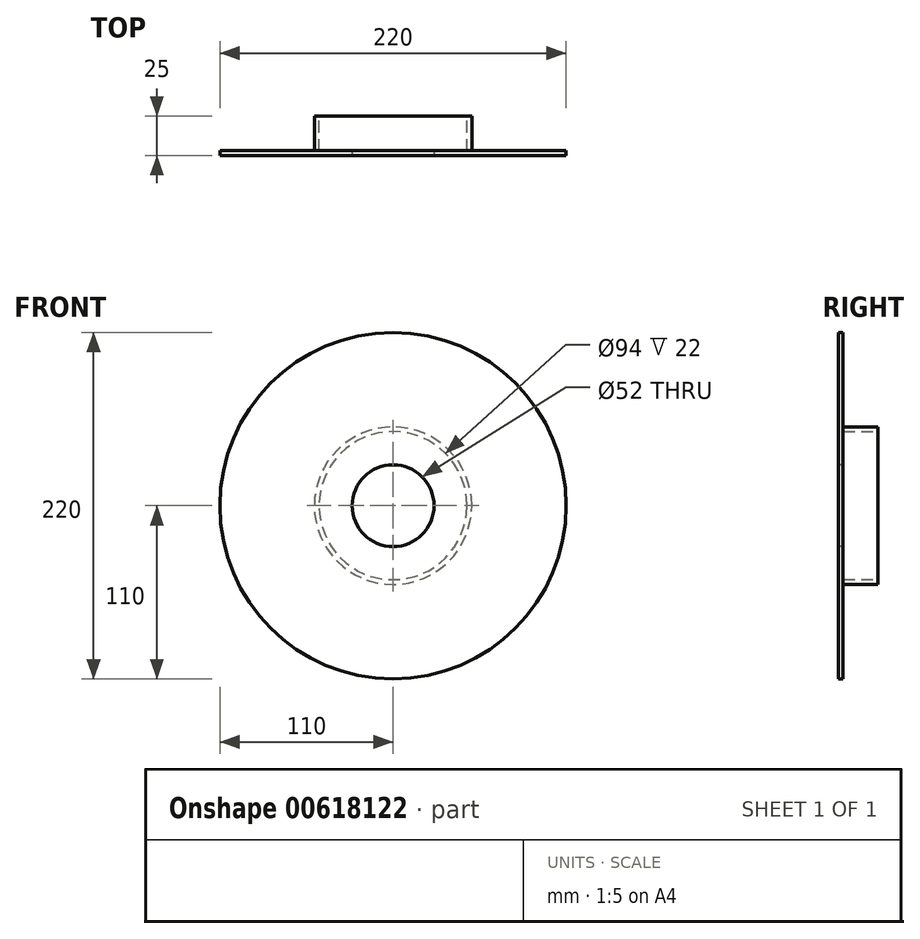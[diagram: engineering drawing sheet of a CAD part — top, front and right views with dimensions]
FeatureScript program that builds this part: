
annotation { "Feature Type Name" : "Feature", "Feature Type Description" : "" }
export const myFeature = defineFeature(function(context is Context, id is Id, definition is map)
    precondition{}
    {
        {
            var Q0;
            Q0=qCreatedBy(makeId("Front.planeOp"),FACE);
            var sketch = newSketch(context, id + "F0", { "sketchPlane" : qUnion([Q0])});
            skCircle(sketch, "E0", {"center": v(0, 0) * mm, "radius": 50 * mm});
            skCircle(sketch, "E1.0", {"center": v(0, 0) * mm, "radius": 47 * mm});
            skCircle(sketch, "E2", {"center": v(0, 0) * mm, "radius": 48.5 * mm});
            skLineSegment(sketch, "E3", {"start": v(0, 47) * mm, "end": v(0, 50) * mm});
            skLineSegment(sketch, "E4", {"start": v(33.23, 33.23) * mm, "end": v(35.36, 35.36) * mm});
            skLineSegment(sketch, "E5.1.0", {"start": v(-47, 0) * mm, "end": v(-50, 0) * mm});
            skLineSegment(sketch, "E5.1.1", {"start": v(-33.23, 33.23) * mm, "end": v(-35.36, 35.36) * mm});
            skLineSegment(sketch, "E5.2.0", {"start": v(0, -47) * mm, "end": v(0, -50) * mm});
            skLineSegment(sketch, "E5.2.1", {"start": v(-33.23, -33.23) * mm, "end": v(-35.36, -35.36) * mm});
            skLineSegment(sketch, "E5.3.0", {"start": v(47, 0) * mm, "end": v(50, 0) * mm});
            skLineSegment(sketch, "E5.3.1", {"start": v(33.23, -33.23) * mm, "end": v(35.36, -35.36) * mm});
            skSolve(sketch);
        }
        {
            var Q0;
            Q0=makeQuery(id+"F0.imprint","IMPRINT",FACE,{"disambiguationData":[TD([[makeQuery(id+"F0.imprint","IMPRINT",EDGE,{"derivedFrom":sQuery(id+"F0.wireOp",EDGE,"E0")}),1.0]])]});
            var Q1;
            {var subQ0=sQuery(id+"F0.wireOp",EDGE,"E3");var subQ1=sQuery(id+"F0.wireOp",EDGE,"E1.0");var subQ2=makeQuery(id+"F0.imprint","INTERSECT",VERTEX,{"derivedFrom":[subQ1,subQ0]});Q1=makeQuery(id+"F0.imprint","IMPRINT",FACE,{"disambiguationData":[TD([[makeQuery(id+"F0.imprint","IMPRINT",EDGE,{"disambiguationData":[TD([[subQ2,-1.0]])],"derivedFrom":subQ1}),-1.0]])]});}
            var Q2;
            {var subQ0=sQuery(id+"F0.wireOp",EDGE,"ee602be9-f56a-464f-86fb-2bc137bb6036.1.0");var subQ1=sQuery(id+"F0.wireOp",EDGE,"E1.0");var subQ2=makeQuery(id+"F0.imprint","INTERSECT",VERTEX,{"derivedFrom":[subQ1,subQ0]});Q2=makeQuery(id+"F0.imprint","IMPRINT",FACE,{"disambiguationData":[TD([[makeQuery(id+"F0.imprint","IMPRINT",EDGE,{"disambiguationData":[TD([[subQ2,1.0]])],"derivedFrom":subQ1}),-1.0]])]});}
            var Q3;
            {var subQ0=sQuery(id+"F0.wireOp",EDGE,"ee602be9-f56a-464f-86fb-2bc137bb6036.1.0");var subQ1=sQuery(id+"F0.wireOp",EDGE,"E1.0");var subQ2=makeQuery(id+"F0.imprint","INTERSECT",VERTEX,{"derivedFrom":[subQ1,subQ0]});Q3=makeQuery(id+"F0.imprint","IMPRINT",FACE,{"disambiguationData":[TD([[makeQuery(id+"F0.imprint","IMPRINT",EDGE,{"disambiguationData":[TD([[subQ2,-1.0]])],"derivedFrom":subQ1}),-1.0]])]});}
            var Q4;
            {var subQ0=sQuery(id+"F0.wireOp",EDGE,"E3");var subQ1=sQuery(id+"F0.wireOp",EDGE,"E1.0");var subQ2=makeQuery(id+"F0.imprint","INTERSECT",VERTEX,{"derivedFrom":[subQ1,subQ0]});Q4=makeQuery(id+"F0.imprint","IMPRINT",FACE,{"disambiguationData":[TD([[makeQuery(id+"F0.imprint","IMPRINT",EDGE,{"disambiguationData":[TD([[subQ2,1.0]])],"derivedFrom":subQ1}),-1.0]])]});}
            var Q5;
            {var subQ0=sQuery(id+"F0.wireOp",EDGE,"ee602be9-f56a-464f-86fb-2bc137bb6036.2.0");var subQ1=sQuery(id+"F0.wireOp",EDGE,"E1.0");var subQ2=makeQuery(id+"F0.imprint","INTERSECT",VERTEX,{"derivedFrom":[subQ1,subQ0]});Q5=makeQuery(id+"F0.imprint","IMPRINT",FACE,{"disambiguationData":[TD([[makeQuery(id+"F0.imprint","IMPRINT",EDGE,{"disambiguationData":[TD([[subQ2,1.0]])],"derivedFrom":subQ1}),-1.0]])]});}
            var Q6;
            {var subQ0=sQuery(id+"F0.wireOp",EDGE,"E4");var subQ1=sQuery(id+"F0.wireOp",EDGE,"E1.0");var subQ2=makeQuery(id+"F0.imprint","INTERSECT",VERTEX,{"derivedFrom":[subQ1,subQ0]});Q6=makeQuery(id+"F0.imprint","IMPRINT",FACE,{"disambiguationData":[TD([[makeQuery(id+"F0.imprint","IMPRINT",EDGE,{"disambiguationData":[TD([[subQ2,1.0]])],"derivedFrom":subQ1}),-1.0]])]});}
            extrude(context, id + "F1", {"entities" : qUnion([Q0, Q1, Q2, Q3, Q4, Q5, Q6]), "depth" : 22 * mm, "offsetDistance" : 25 * mm});
        }
        {
            var Q0;
            Q0=makeQuery(id+"F1.opExtrude","CAP_FACE",FACE,{"disambiguationData":[OSD([sQuery(id+"F0.wireOp",EDGE,"E0")])],"isStart":false});
            var sketch = newSketch(context, id + "F2", { "sketchPlane" : qUnion([Q0])});
            skPoint(sketch, "E6.0", {"position": v(0, 0) * mm});
            skCircle(sketch, "E7", {"center": v(0, 0) * mm, "radius": 110 * mm});
            skSolve(sketch);
        }
        {
            var Q0;
            Q0=makeQuery(id+"F2.imprint","IMPRINT",FACE,{"disambiguationData":[TD([[makeQuery(id+"F2.imprint","IMPRINT",EDGE,{"derivedFrom":sQuery(id+"F2.wireOp",EDGE,"E7")}),1.0]])]});
            var Q1;
            Q1=makeQuery(id+"F2.imprint","IMPRINT",FACE,{"disambiguationData":[TD([[makeQuery(id+"F2.imprint","IMPRINT",EDGE,{"derivedFrom":makeQuery(id+"F1.opExtrude","CAP_EDGE",EDGE,{"disambiguationData":[OSD([sQuery(id+"F0.wireOp",EDGE,"E0")])],"isStart":false})}),1.0]])]});
            var Q2;
            Q2=makeQuery(id+"F2.imprint","IMPRINT",FACE,{"disambiguationData":[TD([[makeQuery(id+"F2.imprint","IMPRINT",EDGE,{"derivedFrom":makeQuery(id+"F1.opExtrude","CAP_EDGE",EDGE,{"disambiguationData":[OSD([sQuery(id+"F0.wireOp",EDGE,"E1.0")])],"isStart":false})}),1.0]])]});
            var Q3;
            Q3=makeQuery(id+"F2.imprint","IMPRINT",FACE,{"disambiguationData":[TD([[makeQuery(id+"F2.imprint","IMPRINT",EDGE,{"derivedFrom":makeQuery(id+"F1.opExtrude","CAP_EDGE",EDGE,{"disambiguationData":[OSD([sQuery(id+"F0.wireOp",EDGE,"E2")])],"isStart":false})}),1.0]])]});
            extrude(context, id + "F3", {"entities" : qUnion([Q0, Q1, Q2, Q3]), "operationType" : NewBodyOperationType.ADD, "depth" : 3 * mm, "offsetDistance" : 25 * mm});
        }
        {
            var Q0;
            Q0=makeQuery(id+"F3.opExtrude","CAP_FACE",FACE,{"disambiguationData":[OSD([sQuery(id+"F2.wireOp",EDGE,"E7")])],"isStart":false});
            var sketch = newSketch(context, id + "F4", { "sketchPlane" : qUnion([Q0])});
            skCircle(sketch, "E8", {"center": v(0, 0) * mm, "radius": 26 * mm});
            skSolve(sketch);
        }
        {
            var Q0;
            Q0=makeQuery(id+"F4.imprint","IMPRINT",FACE,{"disambiguationData":[TD([[makeQuery(id+"F4.imprint","IMPRINT",EDGE,{"derivedFrom":sQuery(id+"F4.wireOp",EDGE,"E8")}),1.0]])]});
            extrude(context, id + "F5", {"entities" : qUnion([Q0]), "operationType" : NewBodyOperationType.REMOVE, "endBound" : BoundingType.UP_TO_NEXT, "oppositeDirection" : true, "depth" : 25 * mm, "offsetDistance" : 25 * mm});
        }
        {
            var Q0;
            Q0 = qSketchRegion(id + "F0", true);
            extrude(context, id + "F6", {"entities" : qUnion([Q0]), "operationType" : NewBodyOperationType.ADD, "depth" : 25 * mm, "offsetDistance" : 25 * mm});
        }
    });
